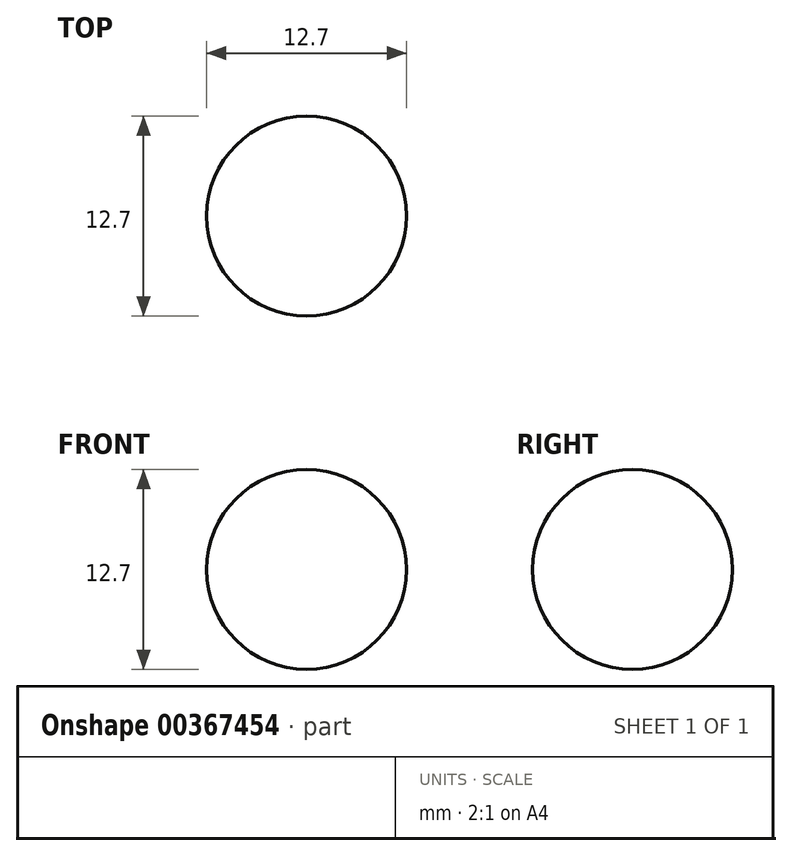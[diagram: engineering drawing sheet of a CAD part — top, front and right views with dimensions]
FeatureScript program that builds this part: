
annotation { "Feature Type Name" : "Feature", "Feature Type Description" : "" }
export const myFeature = defineFeature(function(context is Context, id is Id, definition is map)
    precondition{}
    {
        {
            var Q0;
            Q0=qCreatedBy(makeId("Front.planeOp"),FACE);
            var sketch = newSketch(context, id + "F0", { "sketchPlane" : qUnion([Q0])});
            skArc(sketch, "E0", {"start": v(0, -6.35) * mm, "mid": v(6.35, 0) * mm, "end": v(0, 6.35) * mm});
            skLineSegment(sketch, "E1", {"start": v(0, 6.35) * mm, "end": v(0, -6.35) * mm});
            skSolve(sketch);
        }
        {
            var Q0;
            Q0=qSketchRegion(id+"F0",true);
            var Q1;
            Q1=sQuery(id+"F0.wireOp",EDGE,"E1");
            revolve(context, id + "F1", {"entities" : qUnion([Q0]), "axis" : qUnion([Q1]), "revolveType" : RevolveType.FULL});
        }
    });
